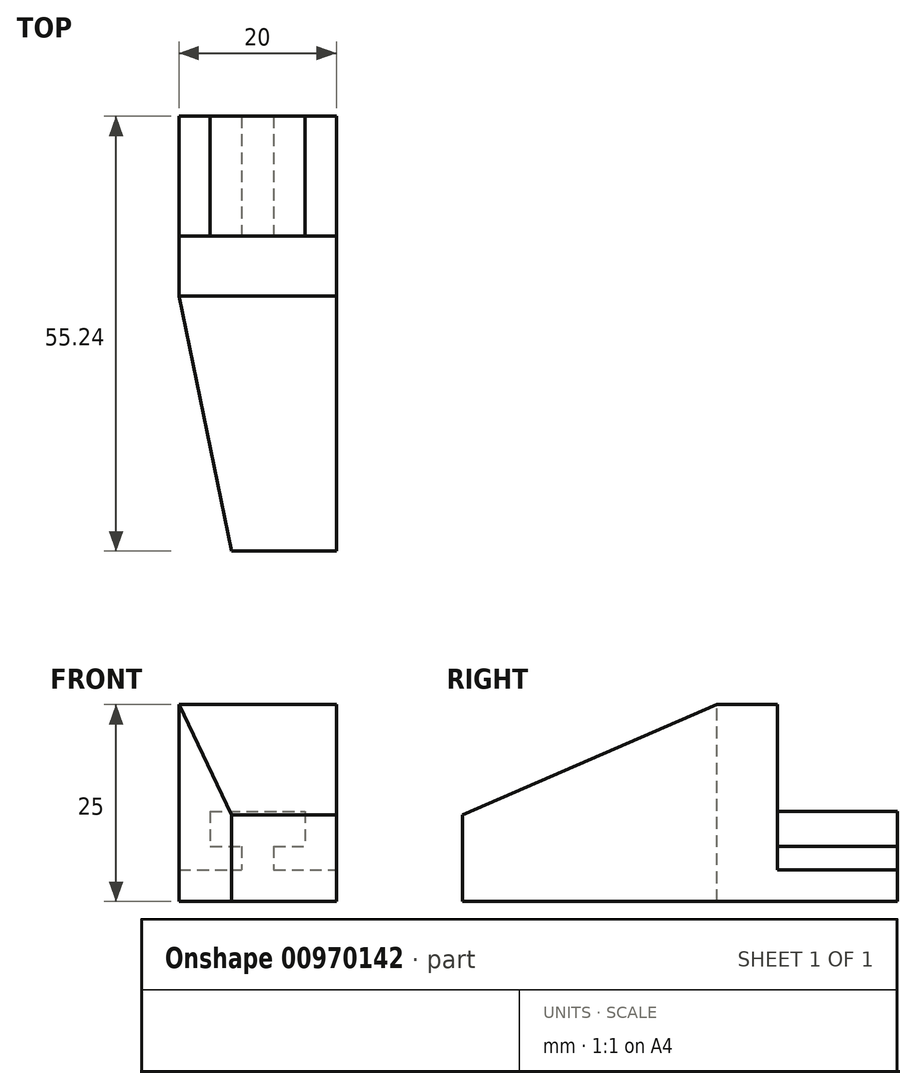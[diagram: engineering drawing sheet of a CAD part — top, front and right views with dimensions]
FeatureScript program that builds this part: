
annotation { "Feature Type Name" : "Feature", "Feature Type Description" : "" }
export const myFeature = defineFeature(function(context is Context, id is Id, definition is map)
    precondition{}
    {
        {
            var Q0;
            Q0=qCreatedBy(makeId("Front.planeOp"),FACE);
            var sketch = newSketch(context, id + "F0", { "sketchPlane" : qUnion([Q0])});
            skLineSegment(sketch, "E0.bottom", {"start": v(-6.03, 4.45) * mm, "end": v(6.03, 4.45) * mm});
            skLineSegment(sketch, "E0.top", {"start": v(-6.03, 0) * mm, "end": v(6.03, 0) * mm});
            skLineSegment(sketch, "E0.left", {"start": v(-6.03, 4.44) * mm, "end": v(-6.03, 0) * mm});
            skLineSegment(sketch, "E0.right", {"start": v(6.03, 4.45) * mm, "end": v(6.03, 0) * mm});
            skLineSegment(sketch, "E1.bottom", {"start": v(2.03, 0) * mm, "end": v(-2.03, 0) * mm});
            skLineSegment(sketch, "E1.top", {"start": v(2.03, -3) * mm, "end": v(-2.03, -3) * mm});
            skLineSegment(sketch, "E1.left", {"start": v(2.03, 0) * mm, "end": v(2.03, -3) * mm});
            skLineSegment(sketch, "E1.right", {"start": v(-2.03, 0) * mm, "end": v(-2.03, -3) * mm});
            skLineSegment(sketch, "E2.bottom", {"start": v(-10, -3) * mm, "end": v(10, -3) * mm});
            skLineSegment(sketch, "E2.top", {"start": v(-10, -7) * mm, "end": v(10, -7) * mm});
            skLineSegment(sketch, "E2.left", {"start": v(-10, -3) * mm, "end": v(-10, -7) * mm});
            skLineSegment(sketch, "E2.right", {"start": v(10, -3) * mm, "end": v(10, -7) * mm});
            skPoint(sketch, "E3", {"position": v(0, 0) * mm});
            skPoint(sketch, "E4", {"position": v(0, -3) * mm});
            skSolve(sketch);
        }
        {
            var Q0;
            Q0 = qSketchRegion(id + "F0", true);
            extrude(context, id + "F1", {"entities" : qUnion([Q0]), "oppositeDirection" : true, "depth" : 15.24 * mm, "offsetDistance" : 25 * mm});
        }
        {
            var Q0;
            Q0=makeQuery(id+"F1.opExtrude","CAP_FACE",FACE,{"disambiguationData":[OSD([sQuery(id+"F0.wireOp",EDGE,"E0.bottom"),sQuery(id+"F0.wireOp",EDGE,"E0.top"),sQuery(id+"F0.wireOp",EDGE,"E0.left"),sQuery(id+"F0.wireOp",EDGE,"E0.right"),sQuery(id+"F0.wireOp",EDGE,"E1.left"),sQuery(id+"F0.wireOp",EDGE,"E1.right"),sQuery(id+"F0.wireOp",EDGE,"E2.bottom"),sQuery(id+"F0.wireOp",EDGE,"E2.top"),sQuery(id+"F0.wireOp",EDGE,"E2.left"),sQuery(id+"F0.wireOp",EDGE,"E2.right")])],"isStart":true});
            var sketch = newSketch(context, id + "F2", { "sketchPlane" : qUnion([Q0])});
            skLineSegment(sketch, "E5.bottom", {"start": v(10, -7) * mm, "end": v(-10, -7) * mm});
            skLineSegment(sketch, "E5.top", {"start": v(10, 18) * mm, "end": v(-10, 18) * mm});
            skLineSegment(sketch, "E5.left", {"start": v(10, -7) * mm, "end": v(10, 18) * mm});
            skLineSegment(sketch, "E5.right", {"start": v(-10, -7) * mm, "end": v(-10, 18) * mm});
            skSolve(sketch);
        }
        {
            var Q0;
            Q0 = qSketchRegion(id + "F2", true);
            extrude(context, id + "F3", {"entities" : qUnion([Q0]), "operationType" : NewBodyOperationType.ADD, "depth" : 40 * mm, "offsetDistance" : 25 * mm});
        }
        {
            var Q0;
            Q0=makeQuery(id+"F3.opExtrude","SWEPT_FACE",FACE,{"disambiguationData":[OSD([sQuery(id+"F2.wireOp",EDGE,"E5.top")])]});
            var sketch = newSketch(context, id + "F4", { "sketchPlane" : qUnion([Q0])});
            skLineSegment(sketch, "E6", {"start": v(-10, -7.64) * mm, "end": v(-3.3, -40) * mm});
            skSolve(sketch);
        }
        {
            var Q0;
            {var subQ0=sQuery(id+"F4.wireOp",EDGE,"E6");Q0=makeQuery(id+"F4.imprint","IMPRINT",FACE,{"disambiguationData":[TD([[makeQuery(id+"F4.imprint","IMPRINT",EDGE,{"derivedFrom":subQ0}),-1.0]])]});}
            extrude(context, id + "F5", {"entities" : qUnion([Q0]), "operationType" : NewBodyOperationType.REMOVE, "endBound" : BoundingType.THROUGH_ALL, "oppositeDirection" : true, "depth" : 25 * mm, "offsetDistance" : 25 * mm});
        }
        {
            var Q0;
            Q0=makeQuery(id+"F3.boolean.opBoolean","MERGE",FACE,{"derivedFrom":[makeQuery(id+"F1.opExtrude","SWEPT_FACE",FACE,{"disambiguationData":[OSD([sQuery(id+"F0.wireOp",EDGE,"E2.right")])]}),makeQuery(id+"F3.opExtrude","SWEPT_FACE",FACE,{"disambiguationData":[OSD([sQuery(id+"F2.wireOp",EDGE,"E5.left")])]})]});
            var sketch = newSketch(context, id + "F6", { "sketchPlane" : qUnion([Q0])});
            skLineSegment(sketch, "E7.0", {"start": v(-40, -7) * mm, "end": v(-7.64, -7) * mm});
            skLineSegment(sketch, "E8.0", {"start": v(-7.64, -7) * mm, "end": v(-7.64, 18) * mm});
            skLineSegment(sketch, "E9", {"start": v(-40, -7) * mm, "end": v(-40, 4) * mm});
            skLineSegment(sketch, "E10", {"start": v(-40, 4) * mm, "end": v(-7.64, 18) * mm});
            skLineSegment(sketch, "E11", {"start": v(-40, 4) * mm, "end": v(-40, 18) * mm});
            skLineSegment(sketch, "E12", {"start": v(-40, 18) * mm, "end": v(-7.64, 18) * mm});
            skSolve(sketch);
        }
        {
            var Q0;
            Q0=makeQuery(id+"F6.imprint","IMPRINT",FACE,{"disambiguationData":[TD([[makeQuery(id+"F6.imprint","IMPRINT",EDGE,{"derivedFrom":sQuery(id+"F6.wireOp",EDGE,"E10")}),1.0]])]});
            extrude(context, id + "F7", {"entities" : qUnion([Q0]), "operationType" : NewBodyOperationType.REMOVE, "endBound" : BoundingType.THROUGH_ALL, "oppositeDirection" : true, "depth" : 25 * mm, "offsetDistance" : 25 * mm});
        }
    });
